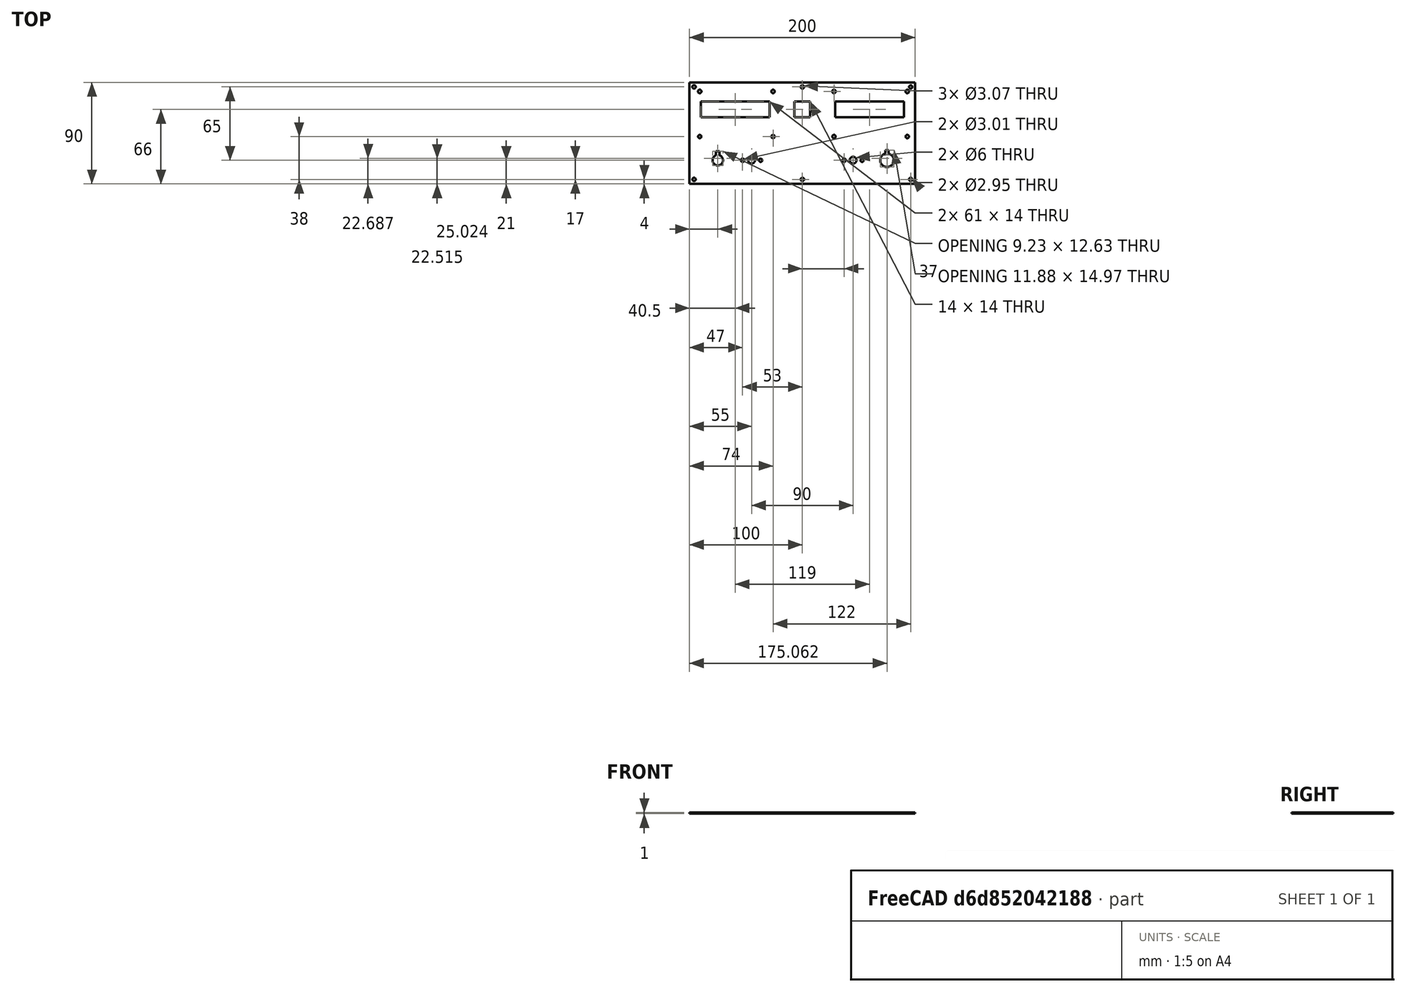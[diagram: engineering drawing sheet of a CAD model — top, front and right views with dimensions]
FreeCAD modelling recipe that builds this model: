
FCSTD DOCUMENT  (FreeCAD 0.18R16161 (Git))
Label: FrontPanelV1
License: All rights reserved
LicenseURL: http://en.wikipedia.org/wiki/All_rights_reserved
objects: Part::Box×2, Part::Cut×2, Sketcher::SketchObject×1, PartDesign::Pad×1, PartDesign::Body×1
note: 8 computed .brp shape members not serialized (recipe doc carries the construction recipe); baked Part::Feature solids carry a one-line shape summary decoded from their .brp

FEATURE [Sketcher::SketchObject] Sketch
  MapMode = 5
  Support = -> [XY_Plane]
  sketch-geometry (38):
    g0: LineSegment StartX=0 StartY=0 StartZ=0 EndX=200 EndY=0 EndZ=0
    g1: LineSegment StartX=200 StartY=0 StartZ=0 EndX=200 EndY=90 EndZ=0
    g2: LineSegment StartX=200 StartY=90 StartZ=0 EndX=0 EndY=90 EndZ=0
    g3: LineSegment StartX=0 StartY=90 StartZ=0 EndX=0 EndY=0 EndZ=0
    g4: LineSegment StartX=10 StartY=73 StartZ=0 EndX=71 EndY=73 EndZ=0
    g5: LineSegment StartX=71 StartY=73 StartZ=0 EndX=71 EndY=59 EndZ=0
    g6: LineSegment StartX=71 StartY=59 StartZ=0 EndX=10 EndY=59 EndZ=0
    g7: LineSegment StartX=10 StartY=59 StartZ=0 EndX=10 EndY=73 EndZ=0
    g8: LineSegment StartX=93 StartY=73 StartZ=0 EndX=107 EndY=73 EndZ=0
    g9: LineSegment StartX=107 StartY=73 StartZ=0 EndX=107 EndY=59 EndZ=0
    g10: LineSegment StartX=107 StartY=59 StartZ=0 EndX=93 EndY=59 EndZ=0
    g11: LineSegment StartX=93 StartY=59 StartZ=0 EndX=93 EndY=73 EndZ=0
    g12: LineSegment StartX=129 StartY=73 StartZ=0 EndX=190 EndY=73 EndZ=0
    g13: LineSegment StartX=190 StartY=73 StartZ=0 EndX=190 EndY=59 EndZ=0
    g14: LineSegment StartX=190 StartY=59 StartZ=0 EndX=129 EndY=59 EndZ=0
    g15: LineSegment StartX=129 StartY=59 StartZ=0 EndX=129 EndY=73 EndZ=0
    g16: Circle CenterX=9 CenterY=82 CenterZ=0 NormalX=0 NormalY=0 NormalZ=1 AngleXU=0 Radius=1.54985
    g17: Circle CenterX=128 CenterY=82 CenterZ=0 NormalX=0 NormalY=0 NormalZ=1 AngleXU=0 Radius=1.53471
    g18: Circle CenterX=9 CenterY=42 CenterZ=0 NormalX=0 NormalY=0 NormalZ=1 AngleXU=0 Radius=1.45036
    g19: Circle CenterX=128 CenterY=42 CenterZ=0 NormalX=0 NormalY=0 NormalZ=1 AngleXU=0 Radius=1.48704
    g20: Circle CenterX=74 CenterY=82 CenterZ=0 NormalX=0 NormalY=0 NormalZ=1 AngleXU=0 Radius=1.5
    g21: Circle CenterX=193 CenterY=82 CenterZ=0 NormalX=0 NormalY=0 NormalZ=1 AngleXU=0 Radius=1.54638
    g22: Circle CenterX=74 CenterY=42 CenterZ=0 NormalX=0 NormalY=0 NormalZ=1 AngleXU=0 Radius=1.47581
    g23: Circle CenterX=193 CenterY=42 CenterZ=0 NormalX=0 NormalY=0 NormalZ=1 AngleXU=0 Radius=1.47087
    g24: Circle CenterX=4 CenterY=86 CenterZ=0 NormalX=0 NormalY=0 NormalZ=1 AngleXU=0 Radius=1.51778
    g25: Circle CenterX=196 CenterY=86 CenterZ=0 NormalX=0 NormalY=0 NormalZ=1 AngleXU=0 Radius=1.45947
    g26: Circle CenterX=196 CenterY=4 CenterZ=0 NormalX=0 NormalY=0 NormalZ=1 AngleXU=0 Radius=1.47405
    g27: Circle CenterX=4 CenterY=4 CenterZ=0 NormalX=0 NormalY=0 NormalZ=1 AngleXU=0 Radius=1.45286
    g28: Circle CenterX=100 CenterY=4 CenterZ=0 NormalX=0 NormalY=0 NormalZ=1 AngleXU=0 Radius=1.50738
    g29: Circle CenterX=100 CenterY=86 CenterZ=0 NormalX=0 NormalY=0 NormalZ=1 AngleXU=0 Radius=1.53256
    g30: Circle CenterX=25 CenterY=21 CenterZ=0 NormalX=0 NormalY=0 NormalZ=1 AngleXU=0 Radius=4.63862
    g31: Circle CenterX=55 CenterY=21 CenterZ=0 NormalX=0 NormalY=0 NormalZ=1 AngleXU=0 Radius=3
    g32: Circle CenterX=63 CenterY=21 CenterZ=0 NormalX=0 NormalY=0 NormalZ=1 AngleXU=0 Radius=1.46953
    g33: Circle CenterX=47 CenterY=21 CenterZ=0 NormalX=0 NormalY=0 NormalZ=1 AngleXU=0 Radius=1.50321
    g34: Circle CenterX=145 CenterY=21 CenterZ=0 NormalX=0 NormalY=0 NormalZ=1 AngleXU=0 Radius=3
    g35: Circle CenterX=153 CenterY=21 CenterZ=0 NormalX=0 NormalY=0 NormalZ=1 AngleXU=0 Radius=1.49249
    g36: Circle CenterX=137 CenterY=21 CenterZ=0 NormalX=0 NormalY=0 NormalZ=1 AngleXU=0 Radius=1.53474
    g37: Circle CenterX=175 CenterY=21 CenterZ=0 NormalX=0 NormalY=0 NormalZ=1 AngleXU=0 Radius=6
  constraints (33):
    c: Coincident(g0,g1)
    c: Coincident(g1,g2)
    c: Coincident(g2,g3)
    c: Coincident(g3,g0)
    c: Horizontal(g0)
    c: Horizontal(g2)
    c: Vertical(g1)
    c: Vertical(g3)
    c: Coincident(g0,g-1)
    c: Coincident(g4,g5)
    c: Coincident(g5,g6)
    c: Coincident(g6,g7)
    c: Coincident(g7,g4)
    c: Horizontal(g4)
    c: Horizontal(g6)
    c: Vertical(g5)
    c: Vertical(g7)
    c: Coincident(g8,g9)
    c: Coincident(g9,g10)
    c: Coincident(g10,g11)
    c: Coincident(g11,g8)
    c: Horizontal(g8)
    c: Horizontal(g10)
    c: Vertical(g9)
    c: Vertical(g11)
    c: Coincident(g12,g13)
    c: Coincident(g13,g14)
    c: Coincident(g14,g15)
    c: Coincident(g15,g12)
    c: Horizontal(g12)
    c: Horizontal(g14)
    c: Vertical(g13)
    c: Vertical(g15)
FEATURE [PartDesign::Pad] Pad
  Length = 1
  Length2 = 100
  Profile = -> Sketch
  Type = 0
FEATURE [PartDesign::Body] Body
  Group = -> [Sketch,Pad]
  Origin = -> Origin
  Tip = -> Pad
FEATURE [Part::Box] Box  label="Cube"
  AttacherType = Attacher::AttachEngine3D
  Height = 15
  Length = 3
  Placement = pos=(23.5,25,-7) rot=(0,0,1;0rad)
  Width = 4
FEATURE [Part::Box] Box001  label="Cube001"
  AttacherType = Attacher::AttachEngine3D
  Height = 15
  Length = 3
  Placement = pos=(173.5,26,-7) rot=(0,0,1;0rad)
  Width = 4
FEATURE [Part::Cut] Cut
  Base = -> Body
  Tool = -> Box
FEATURE [Part::Cut] Cut001
  Base = -> Cut
  Tool = -> Box001
